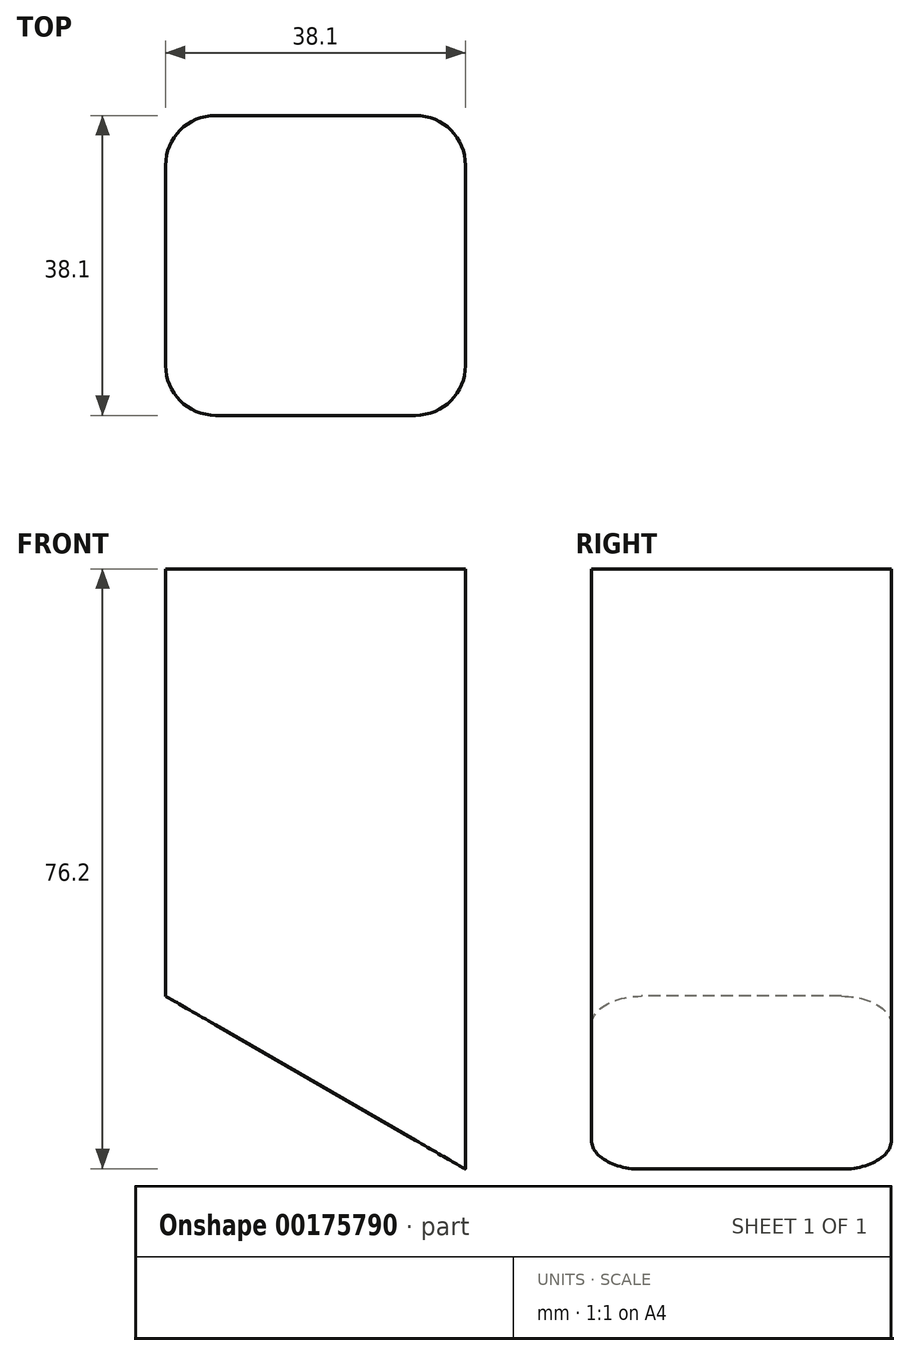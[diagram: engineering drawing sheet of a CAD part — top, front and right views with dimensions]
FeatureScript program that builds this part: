
annotation { "Feature Type Name" : "Feature", "Feature Type Description" : "" }
export const myFeature = defineFeature(function(context is Context, id is Id, definition is map)
    precondition{}
    {
        {
            var Q0;
            Q0=qCreatedBy(makeId("Top.planeOp"),FACE);
            var sketch = newSketch(context, id + "F0", { "sketchPlane" : qUnion([Q0])});
            skLineSegment(sketch, "E0.bottom", {"start": v(12.7, 19.05) * mm, "end": v(-12.7, 19.05) * mm});
            skLineSegment(sketch, "E0.top", {"start": v(12.7, -19.05) * mm, "end": v(-12.7, -19.05) * mm});
            skLineSegment(sketch, "E0.left", {"start": v(19.05, 12.7) * mm, "end": v(19.05, -12.7) * mm});
            skLineSegment(sketch, "E0.right", {"start": v(-19.05, 12.7) * mm, "end": v(-19.05, -12.7) * mm});
            skPoint(sketch, "E0.middle", {"position": v(0, 0) * mm});
            skPoint(sketch, "E1.visualSharp", {"position": v(-19.05, 19.05) * mm});
            skArc(sketch, "E1.filletArc", {"start": v(-12.7, 19.05) * mm, "mid": v(-17.2, 17.2) * mm, "end": v(-19.05, 12.7) * mm});
            skPoint(sketch, "E2.visualSharp", {"position": v(19.05, 19.05) * mm});
            skArc(sketch, "E2.filletArc", {"start": v(19.05, 12.7) * mm, "mid": v(17.2, 17.2) * mm, "end": v(12.7, 19.05) * mm});
            skPoint(sketch, "E3.visualSharp", {"position": v(19.05, -19.05) * mm});
            skArc(sketch, "E3.filletArc", {"start": v(12.7, -19.05) * mm, "mid": v(17.2, -17.2) * mm, "end": v(19.05, -12.7) * mm});
            skPoint(sketch, "E4.visualSharp", {"position": v(-19.05, -19.05) * mm});
            skArc(sketch, "E4.filletArc", {"start": v(-19.05, -12.7) * mm, "mid": v(-17.2, -17.2) * mm, "end": v(-12.7, -19.05) * mm});
            skSolve(sketch);
        }
        {
            var Q0;
            Q0=qSketchRegion(id+"F0",true);
            extrude(context, id + "F1", {"entities" : qUnion([Q0]), "depth" : 76.2 * mm, "offsetDistance" : 25.4 * mm});
        }
        {
            var Q0;
            Q0=qCreatedBy(makeId("Front.planeOp"),FACE);
            var sketch = newSketch(context, id + "F2", { "sketchPlane" : qUnion([Q0])});
            skLineSegment(sketch, "E5", {"start": v(-19.05, 21.92) * mm, "end": v(18.92, 0) * mm});
            skLineSegment(sketch, "E6", {"start": v(18.92, 0) * mm, "end": v(-19.05, 0) * mm});
            skLineSegment(sketch, "E7", {"start": v(-19.05, 0) * mm, "end": v(-19.05, 21.92) * mm});
            skSolve(sketch);
        }
        {
            var Q0;
            Q0 = qSketchRegion(id + "F2", true);
            extrude(context, id + "F3", {"entities" : qUnion([Q0]), "operationType" : NewBodyOperationType.REMOVE, "endBound" : BoundingType.SYMMETRIC, "oppositeDirection" : true, "depth" : 38.1 * mm, "offsetDistance" : 25.4 * mm});
        }
    });
